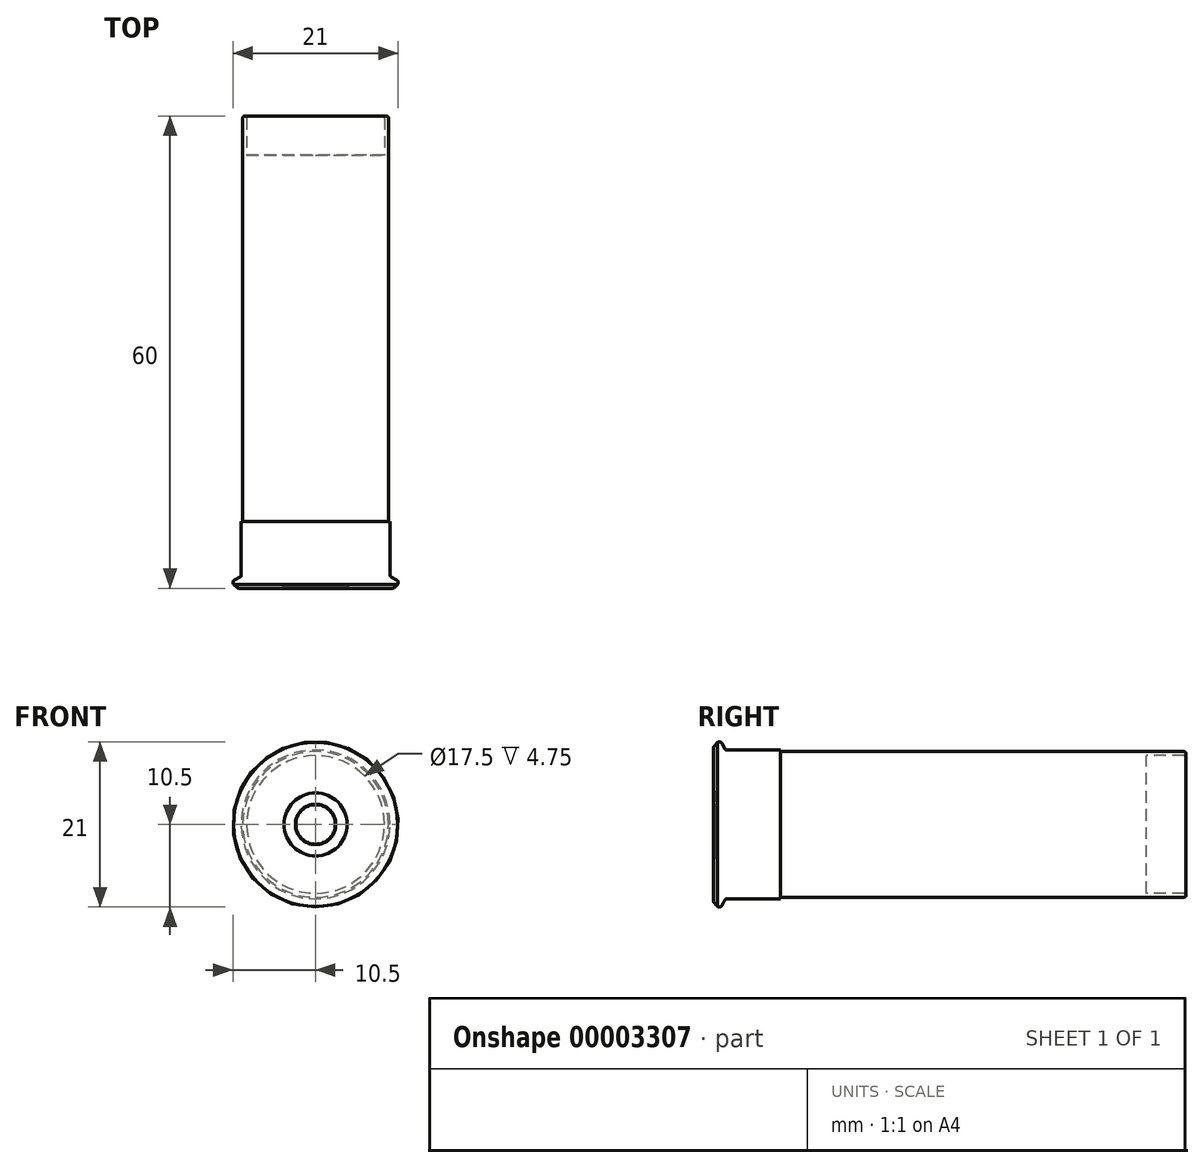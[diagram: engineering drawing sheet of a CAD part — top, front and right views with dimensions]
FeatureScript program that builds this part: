
annotation { "Feature Type Name" : "Feature", "Feature Type Description" : "" }
export const myFeature = defineFeature(function(context is Context, id is Id, definition is map)
    precondition{}
    {
        {
            var Q0;
            Q0=qCreatedBy(makeId("Front.planeOp"),FACE);
            var sketch = newSketch(context, id + "F0", { "sketchPlane" : qUnion([Q0])});
            skCircle(sketch, "E0", {"center": v(0, 0) * mm, "radius": 9.25 * mm});
            skSolve(sketch);
        }
        {
            var Q0;
            Q0=qCreatedBy(makeId("Top.planeOp"),FACE);
            var sketch = newSketch(context, id + "F1", { "sketchPlane" : qUnion([Q0])});
            skLineSegment(sketch, "E1", {"start": v(0, -28.18) * mm, "end": v(0, 60) * mm, "construction": true});
            skLineSegment(sketch, "E2", {"start": v(0, 60) * mm, "end": v(-9.25, 60) * mm, "construction": true});
            skLineSegment(sketch, "E3.0.MirrorCS", {"start": v(0, 60) * mm, "end": v(9.25, 60) * mm, "construction": true});
            skPoint(sketch, "E4", {"position": v(0, 8.5) * mm});
            skLineSegment(sketch, "E5", {"start": v(0, 8.5) * mm, "end": v(-31.72, 8.5) * mm, "construction": true});
            skPoint(sketch, "E6", {"position": v(0, 1.5) * mm});
            skLineSegment(sketch, "E7", {"start": v(0, 1.5) * mm, "end": v(-31.43, 1.5) * mm, "construction": true});
            skPoint(sketch, "E8", {"position": v(0, 0.9) * mm});
            skLineSegment(sketch, "E9", {"start": v(-9.25, 59.75) * mm, "end": v(-9.25, 8.5) * mm});
            skLineSegment(sketch, "E10", {"start": v(-9.45, 8.5) * mm, "end": v(-9.45, 1.68) * mm});
            skLineSegment(sketch, "E11", {"start": v(0, 0) * mm, "end": v(0, 55) * mm});
            skLineSegment(sketch, "E12", {"start": v(-9, 60) * mm, "end": v(-9, 60) * mm});
            skPoint(sketch, "E13.visualSharp", {"position": v(-10.6, 0.9) * mm});
            skPoint(sketch, "E14.visualSharp", {"position": v(-9.89, 0) * mm});
            skPoint(sketch, "E15.visualSharp", {"position": v(-9.45, 1.5) * mm});
            skLineSegment(sketch, "E16", {"start": v(-10.28, 1.07) * mm, "end": v(-9.61, 1.42) * mm});
            skArc(sketch, "E17.filletArc", {"start": v(-10.28, 1.07) * mm, "mid": v(-10.49, 0.8) * mm, "end": v(-10.4, 0.46) * mm});
            skLineSegment(sketch, "E18", {"start": v(-10.4, 0.46) * mm, "end": v(-10, 0.1) * mm});
            skArc(sketch, "E19.filletArc", {"start": v(-10, 0.1) * mm, "mid": v(-9.88, 0.03) * mm, "end": v(-9.74, 0) * mm});
            skPoint(sketch, "E20", {"position": v(-4, 0) * mm});
            skPoint(sketch, "E21.0.MirrorP", {"position": v(4, 0) * mm});
            skArc(sketch, "E22.filletArc", {"start": v(-9.61, 1.42) * mm, "mid": v(-9.5, 1.53) * mm, "end": v(-9.45, 1.68) * mm});
            skLineSegment(sketch, "E23.trimOffspring", {"start": v(-3.98, 0) * mm, "end": v(-2.82, 0) * mm});
            skPoint(sketch, "E24", {"position": v(-2.5, 0) * mm});
            skPoint(sketch, "E25.0.MirrorP", {"position": v(2.5, 0) * mm});
            skLineSegment(sketch, "E26", {"start": v(-9.74, 0) * mm, "end": v(-4.51, 0) * mm});
            skLineSegment(sketch, "E27", {"start": v(-4, 0.02) * mm, "end": v(-4, 0.19) * mm});
            skLineSegment(sketch, "E28", {"start": v(-4.07, 0.23) * mm, "end": v(-4.5, 0) * mm});
            skPoint(sketch, "E29.visualSharp", {"position": v(-4, 0.27) * mm});
            skArc(sketch, "E29.filletArc", {"start": v(-4, 0.19) * mm, "mid": v(-4.02, 0.23) * mm, "end": v(-4.07, 0.23) * mm});
            skArc(sketch, "E30.filletArc", {"start": v(-4, 0.02) * mm, "mid": v(-4, 0) * mm, "end": v(-3.98, 0) * mm});
            skPoint(sketch, "E31.visualSharp", {"position": v(-4.5, 0) * mm});
            skArc(sketch, "E31.filletArc", {"start": v(-4.51, 0) * mm, "mid": v(-4.5, 0) * mm, "end": v(-4.5, 0) * mm});
            skLineSegment(sketch, "E32.trimOffspring", {"start": v(-2.26, 0) * mm, "end": v(0, 0) * mm});
            skPoint(sketch, "E33.visualSharp", {"position": v(-2.57, 0) * mm});
            skArc(sketch, "E34.filletArc", {"start": v(-2.82, 0) * mm, "mid": v(-2.64, 0.07) * mm, "end": v(-2.57, 0.25) * mm});
            skArc(sketch, "E35.filletArc", {"start": v(-2.5, 0.24) * mm, "mid": v(-2.43, 0.07) * mm, "end": v(-2.26, 0) * mm});
            skLineSegment(sketch, "E36", {"start": v(-2.57, 0.25) * mm, "end": v(-2.5, 0.24) * mm});
            skLineSegment(sketch, "E37", {"start": v(-8.75, 59.75) * mm, "end": v(-8.75, 55) * mm});
            skLineSegment(sketch, "E38", {"start": v(-8.75, 55) * mm, "end": v(0, 55) * mm});
            skPoint(sketch, "E39.visualSharp", {"position": v(-9.25, 60) * mm});
            skArc(sketch, "E39.filletArc", {"start": v(-9, 60) * mm, "mid": v(-9.18, 59.93) * mm, "end": v(-9.25, 59.75) * mm});
            skPoint(sketch, "E40.visualSharp", {"position": v(-8.75, 60) * mm});
            skArc(sketch, "E40.filletArc", {"start": v(-8.75, 59.75) * mm, "mid": v(-8.82, 59.93) * mm, "end": v(-9, 60) * mm});
            skLineSegment(sketch, "E41", {"start": v(-9.45, 8.5) * mm, "end": v(-9.25, 8.5) * mm});
            skSolve(sketch);
        }
        {
            var Q0;
            Q0=makeQuery(id+"F1.imprint","IMPRINT",FACE,{"disambiguationData":[TD([[makeQuery(id+"F1.imprint","IMPRINT",EDGE,{"derivedFrom":sQuery(id+"F1.wireOp",EDGE,"E9")}),1.0]])]});
            var Q1;
            Q1=sQuery(id+"F1.wireOp",EDGE,"E1");
            revolve(context, id + "F2", {"entities" : qUnion([Q0]), "axis" : qUnion([Q1]), "revolveType" : RevolveType.FULL});
        }
    });
